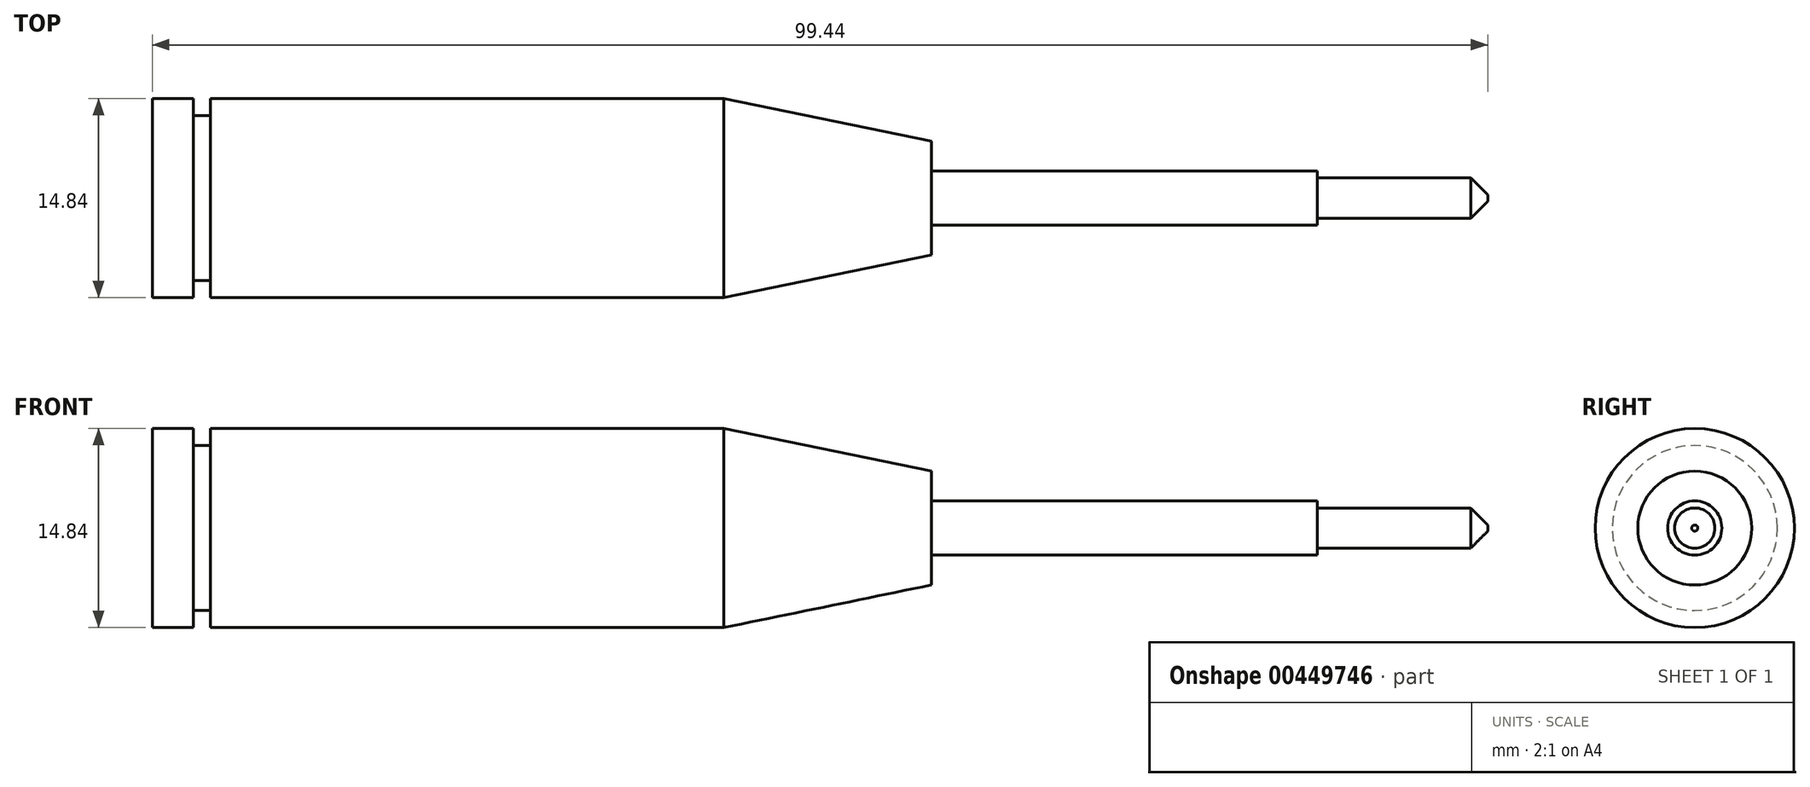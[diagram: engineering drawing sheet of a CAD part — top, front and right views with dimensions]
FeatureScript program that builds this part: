
annotation { "Feature Type Name" : "Feature", "Feature Type Description" : "" }
export const myFeature = defineFeature(function(context is Context, id is Id, definition is map)
    precondition{}
    {
        {
            var Q0;
            Q0=qCreatedBy(makeId("Front.planeOp"),FACE);
            var sketch = newSketch(context, id + "F0", { "sketchPlane" : qUnion([Q0])});
            skLineSegment(sketch, "E0", {"start": v(0, 0) * mm, "end": v(0, 7.42) * mm});
            skLineSegment(sketch, "E1", {"start": v(0, 7.42) * mm, "end": v(3.05, 7.42) * mm});
            skLineSegment(sketch, "E2", {"start": v(3.05, 7.42) * mm, "end": v(3.05, 6.15) * mm});
            skLineSegment(sketch, "E3", {"start": v(3.05, 6.15) * mm, "end": v(4.32, 6.15) * mm});
            skLineSegment(sketch, "E4", {"start": v(4.32, 6.15) * mm, "end": v(4.32, 7.42) * mm});
            skLineSegment(sketch, "E5", {"start": v(4.32, 7.42) * mm, "end": v(42.55, 7.42) * mm});
            skLineSegment(sketch, "E6", {"start": v(42.54, 7.42) * mm, "end": v(58.01, 4.24) * mm});
            skLineSegment(sketch, "E7", {"start": v(58.01, 4.24) * mm, "end": v(58.01, 2.02) * mm});
            skLineSegment(sketch, "E8", {"start": v(58.01, 2.02) * mm, "end": v(86.74, 2.02) * mm});
            skLineSegment(sketch, "E9", {"start": v(86.74, 2.02) * mm, "end": v(86.74, 0) * mm});
            skLineSegment(sketch, "E10", {"start": v(86.74, 0) * mm, "end": v(0, 0) * mm});
            skSolve(sketch);
        }
        {
            var Q0;
            Q0 = qSketchRegion(id + "F0", true);
            var Q1;
            Q1=sQuery(id+"F0.wireOp",EDGE,"E10");
            revolve(context, id + "F1", {"entities" : qUnion([Q0]), "axis" : qUnion([Q1]), "revolveType" : RevolveType.FULL});
        }
        {
            var Q0;
            Q0=makeQuery(id+"F1.opRevolve","SWEPT_FACE",FACE,{"disambiguationData":[OSD([sQuery(id+"F0.wireOp",EDGE,"E9")])]});
            var sketch = newSketch(context, id + "F2", { "sketchPlane" : qUnion([Q0])});
            skCircle(sketch, "E11", {"center": v(0, 0) * mm, "radius": 1.5 * mm});
            skSolve(sketch);
        }
        {
            var Q0;
            Q0 = qSketchRegion(id + "F2", true);
            extrude(context, id + "F3", {"entities" : qUnion([Q0]), "depth" : 12.7 * mm});
        }
        {
            var Q0;
            Q0=makeQuery(id+"F3.opExtrude","CAP_EDGE",EDGE,{"disambiguationData":[OSD([sQuery(id+"F2.wireOp",EDGE,"E11")])],"isStart":false});
            chamfer(context, id + "F4", {"entities" : qUnion([Q0]), "width" : 1.27 * mm, "tangentPropagation" : true});
        }
    });
